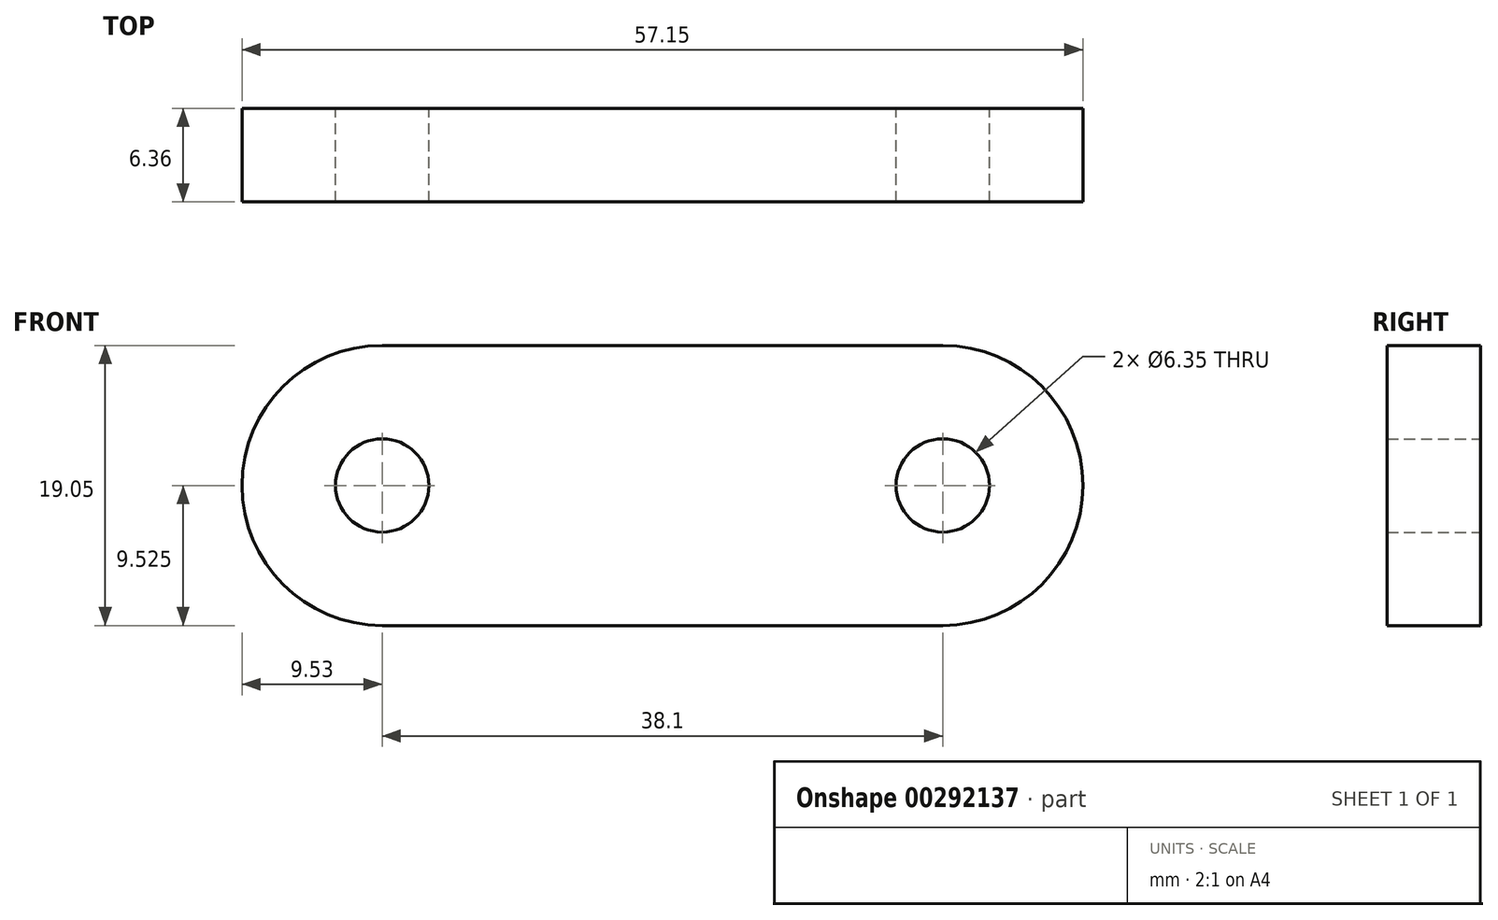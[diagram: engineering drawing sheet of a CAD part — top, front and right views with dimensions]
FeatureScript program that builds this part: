
annotation { "Feature Type Name" : "Feature", "Feature Type Description" : "" }
export const myFeature = defineFeature(function(context is Context, id is Id, definition is map)
    precondition{}
    {
        {
            var Q0;
            Q0=qCreatedBy(makeId("Front.planeOp"),FACE);
            var sketch = newSketch(context, id + "F0", { "sketchPlane" : qUnion([Q0])});
            skLineSegment(sketch, "E0", {"start": v(-23.46, 28.35) * mm, "end": v(14.64, 28.35) * mm});
            skLineSegment(sketch, "E1.0", {"start": v(-23.46, 9.3) * mm, "end": v(14.64, 9.3) * mm});
            skArc(sketch, "E2", {"start": v(-23.46, 28.35) * mm, "mid": v(-32.99, 18.83) * mm, "end": v(-23.46, 9.3) * mm});
            skArc(sketch, "E3", {"start": v(14.64, 28.35) * mm, "mid": v(24.16, 18.83) * mm, "end": v(14.64, 9.3) * mm});
            skCircle(sketch, "E4", {"center": v(-23.46, 18.83) * mm, "radius": 3.18 * mm});
            skCircle(sketch, "E5", {"center": v(14.64, 18.83) * mm, "radius": 3.18 * mm});
            skSolve(sketch);
        }
        {
            var Q0;
            Q0=makeQuery(id+"F0.imprint","IMPRINT",FACE,{"disambiguationData":[TD([[makeQuery(id+"F0.imprint","IMPRINT",EDGE,{"derivedFrom":sQuery(id+"F0.wireOp",EDGE,"E0")}),-1.0]])]});
            extrude(context, id + "F1", {"entities" : qUnion([Q0]), "endBound" : BoundingType.SYMMETRIC, "depth" : 6.35 * mm});
        }
    });
